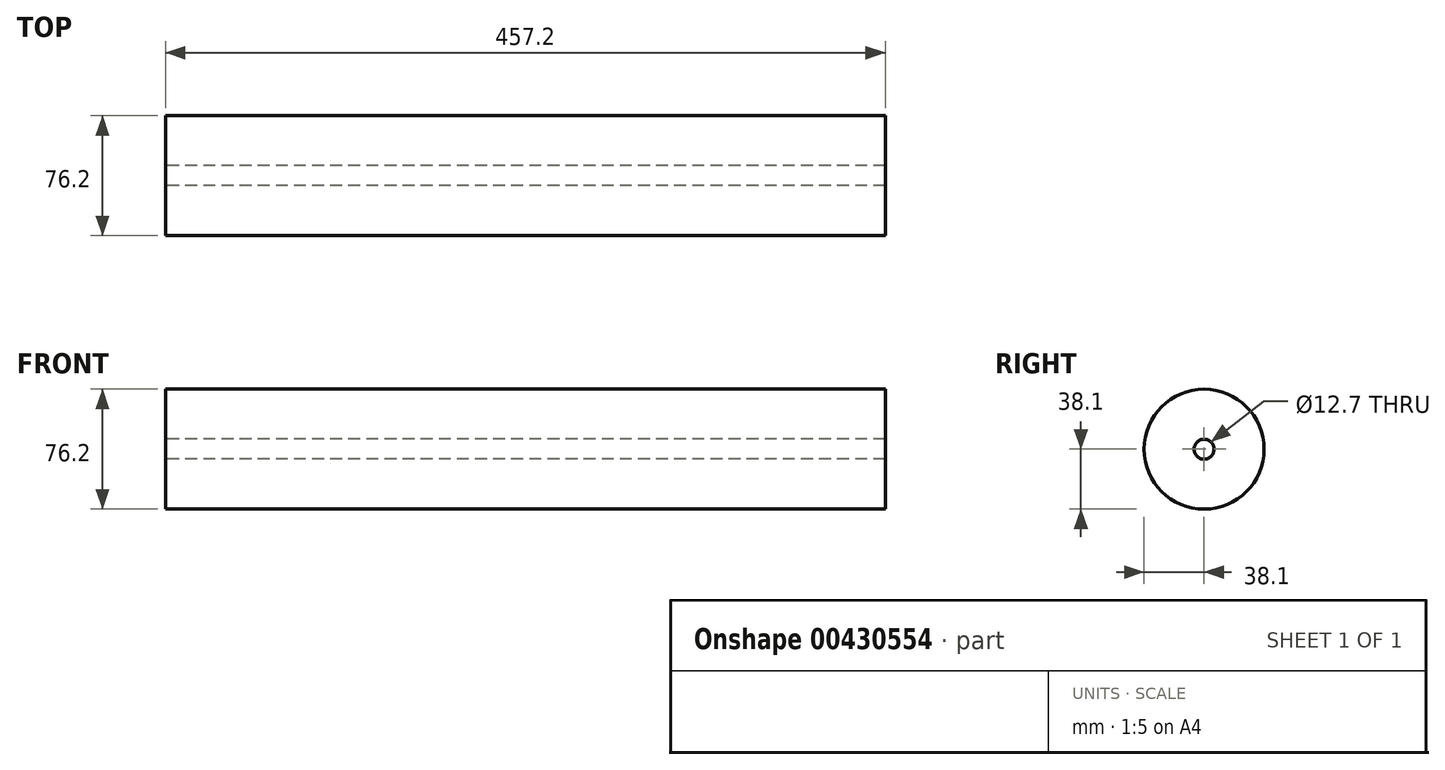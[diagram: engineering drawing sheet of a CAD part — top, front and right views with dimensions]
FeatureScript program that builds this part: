
annotation { "Feature Type Name" : "Feature", "Feature Type Description" : "" }
export const myFeature = defineFeature(function(context is Context, id is Id, definition is map)
    precondition{}
    {
        {
            var Q0;
            Q0=qCreatedBy(makeId("Right.planeOp"),FACE);
            var sketch = newSketch(context, id + "F0", { "sketchPlane" : qUnion([Q0])});
            skCircle(sketch, "E0", {"center": v(0, 0) * mm, "radius": 38.1 * mm});
            skCircle(sketch, "E1", {"center": v(0, 0) * mm, "radius": 6.35 * mm});
            skSolve(sketch);
        }
        {
            var Q0;
            Q0=makeQuery(id+"F0.imprint","IMPRINT",FACE,{"disambiguationData":[TD([[makeQuery(id+"F0.imprint","IMPRINT",EDGE,{"derivedFrom":sQuery(id+"F0.wireOp",EDGE,"E0")}),1.0]])]});
            extrude(context, id + "F1", {"entities" : qUnion([Q0]), "depth" : 457.2 * mm});
        }
    });
